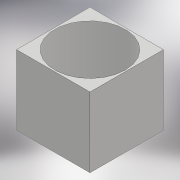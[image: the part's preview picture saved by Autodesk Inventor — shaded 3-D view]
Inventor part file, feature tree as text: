
AUTODESK INVENTOR PART (.ipt)
format: ipt  version: 2018 (Build 220112000, 112)  size: 98,304 bytes
history: native  units: mm
features: extrude x1, sketch x1
ambient origin geometry x8: Origin, YZ Plane, XZ Plane, XY Plane, X Axis, Y Axis, Z Axis, Center Point
bodies: Solid1 (feature_tree)
feature tree (2):
  extrude  "Extrusion1"  Depth=10.5mm
  sketch  "Sketch1"  dims[d0=10.1mm d1=10.5mm d2=10.5mm d3=10.0mm d4=0.0mm]
